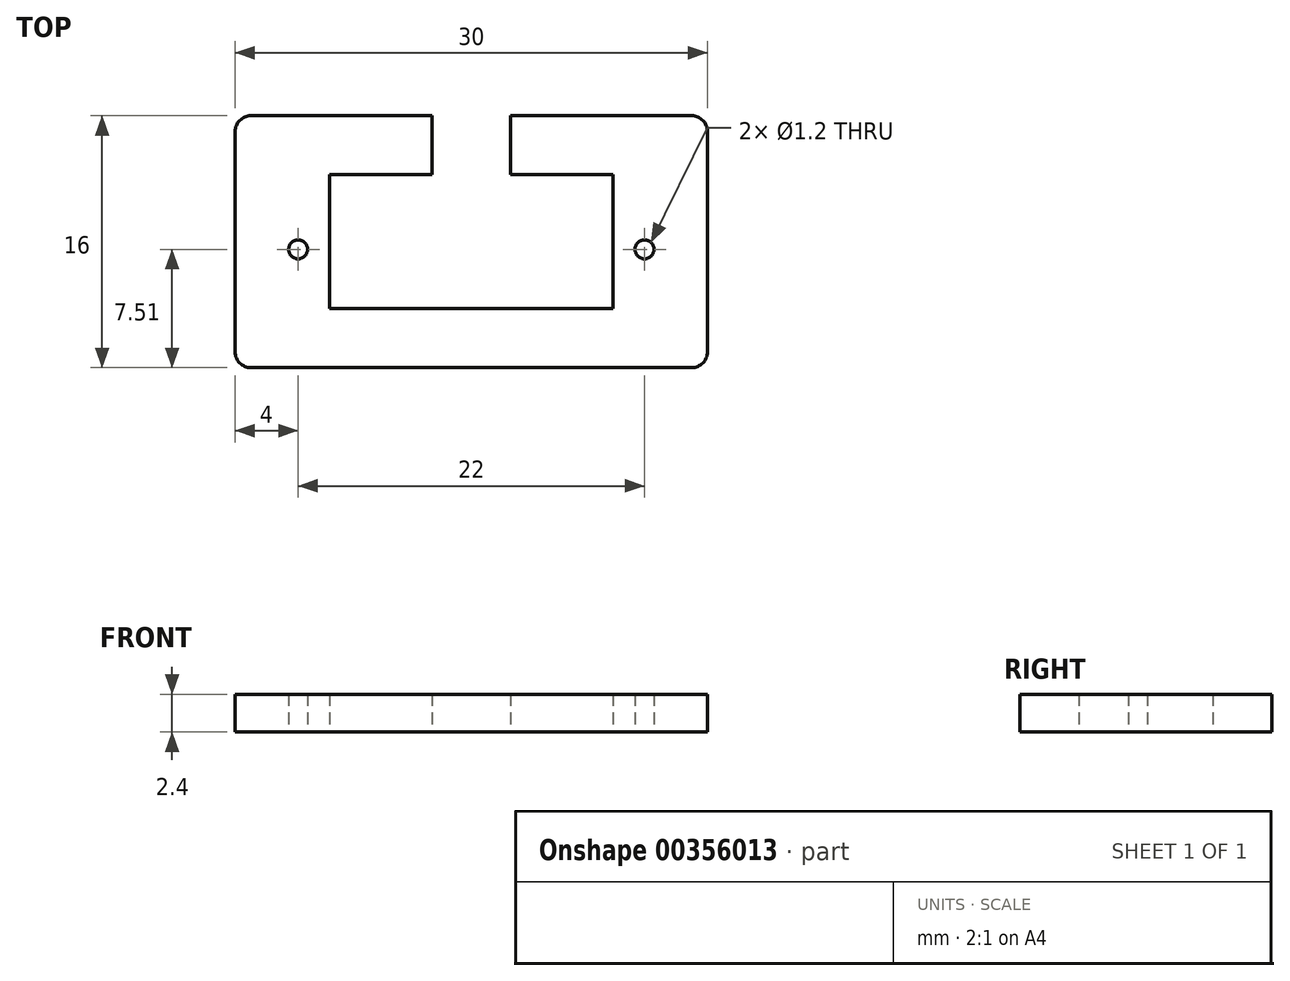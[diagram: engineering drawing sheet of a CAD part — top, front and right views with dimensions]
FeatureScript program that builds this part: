
annotation { "Feature Type Name" : "Feature", "Feature Type Description" : "" }
export const myFeature = defineFeature(function(context is Context, id is Id, definition is map)
    precondition{}
    {
        {
            var Q0;
            Q0=qCreatedBy(makeId("Top.planeOp"),FACE);
            var sketch = newSketch(context, id + "F0", { "sketchPlane" : qUnion([Q0])});
            skLineSegment(sketch, "E0", {"start": v(0, 12.31) * mm, "end": v(0, -11.04) * mm, "construction": true});
            skLineSegment(sketch, "E1", {"start": v(0, 4.74) * mm, "end": v(9, 4.74) * mm});
            skLineSegment(sketch, "E2", {"start": v(9, 4.74) * mm, "end": v(9, -3.76) * mm});
            skLineSegment(sketch, "E3", {"start": v(9, -3.76) * mm, "end": v(0, -3.76) * mm});
            skLineSegment(sketch, "E4", {"start": v(0, 8.5) * mm, "end": v(15, 8.5) * mm});
            skLineSegment(sketch, "E5", {"start": v(15, 8.5) * mm, "end": v(15, -7.5) * mm});
            skLineSegment(sketch, "E6", {"start": v(15, -7.5) * mm, "end": v(0, -7.5) * mm});
            skLineSegment(sketch, "E7.MirrorCS", {"start": v(0, 4.74) * mm, "end": v(-9, 4.74) * mm});
            skLineSegment(sketch, "E8.MirrorCS", {"start": v(0, 8.5) * mm, "end": v(-15, 8.5) * mm});
            skLineSegment(sketch, "E9.MirrorCS", {"start": v(-15, 8.5) * mm, "end": v(-15, -7.5) * mm});
            skLineSegment(sketch, "E10.MirrorCS", {"start": v(-15, -7.5) * mm, "end": v(0, -7.5) * mm});
            skLineSegment(sketch, "E11.MirrorCS", {"start": v(-9, -3.76) * mm, "end": v(0, -3.76) * mm});
            skLineSegment(sketch, "E12.MirrorCS", {"start": v(-9, 4.74) * mm, "end": v(-9, -3.76) * mm});
            skLineSegment(sketch, "E13", {"start": v(0, 8.5) * mm, "end": v(0, 4.74) * mm, "construction": true});
            skLineSegment(sketch, "E14", {"start": v(0, -7.5) * mm, "end": v(0, -3.76) * mm, "construction": true});
            skCircle(sketch, "E15", {"center": v(-11, 0) * mm, "radius": 0.6 * mm});
            skCircle(sketch, "E16.MirrorC", {"center": v(11, 0) * mm, "radius": 0.6 * mm});
            skLineSegment(sketch, "E17.bottom", {"start": v(-2.5, 10.1) * mm, "end": v(0, 10.1) * mm});
            skLineSegment(sketch, "E17.top", {"start": v(-2.5, 3.05) * mm, "end": v(0, 3.05) * mm});
            skLineSegment(sketch, "E17.left", {"start": v(-2.5, 10.1) * mm, "end": v(-2.5, 3.05) * mm});
            skLineSegment(sketch, "E17.right", {"start": v(0, 10.1) * mm, "end": v(0, 3.05) * mm});
            skLineSegment(sketch, "E18.MirrorCS", {"start": v(2.5, 10.1) * mm, "end": v(0, 10.1) * mm});
            skLineSegment(sketch, "E19.MirrorCS", {"start": v(2.5, 3.05) * mm, "end": v(0, 3.05) * mm});
            skLineSegment(sketch, "E20.MirrorCS", {"start": v(2.5, 10.1) * mm, "end": v(2.5, 3.05) * mm});
            skSolve(sketch);
        }
        {
            var Q0;
            {var subQ13=sQuery(id+"F0.wireOp",EDGE,"E2");Q0=makeQuery(id+"F0.imprint","IMPRINT",FACE,{"disambiguationData":[TD([[makeQuery(id+"F0.imprint","IMPRINT",EDGE,{"derivedFrom":subQ13}),1.0]])]});}
            extrude(context, id + "F1", {"entities" : qUnion([Q0]), "depth" : 2.4 * mm});
        }
        {
            var Q0;
            Q0=makeQuery(id+"F1.opExtrude","SWEPT_EDGE",EDGE,{"disambiguationData":[OSD([sQuery(id+"F0.wireOp",EDGE,"E4"),sQuery(id+"F0.wireOp",EDGE,"E5")])]});
            var Q1;
            Q1=makeQuery(id+"F1.opExtrude","SWEPT_EDGE",EDGE,{"disambiguationData":[OSD([sQuery(id+"F0.wireOp",EDGE,"E5"),sQuery(id+"F0.wireOp",EDGE,"E6")])]});
            var Q2;
            Q2=makeQuery(id+"F1.opExtrude","SWEPT_EDGE",EDGE,{"disambiguationData":[OSD([sQuery(id+"F0.wireOp",EDGE,"E8.MirrorCS"),sQuery(id+"F0.wireOp",EDGE,"E9.MirrorCS")])]});
            var Q3;
            Q3=makeQuery(id+"F1.opExtrude","SWEPT_EDGE",EDGE,{"disambiguationData":[OSD([sQuery(id+"F0.wireOp",EDGE,"E9.MirrorCS"),sQuery(id+"F0.wireOp",EDGE,"E10.MirrorCS")])]});
            fillet(context, id + "F2", {"entities" : qUnion([Q0, Q1, Q2, Q3]), "radius" : 1 * mm, "tangentPropagation" : true, "allowEdgeOverflow" : false});
        }
    });
